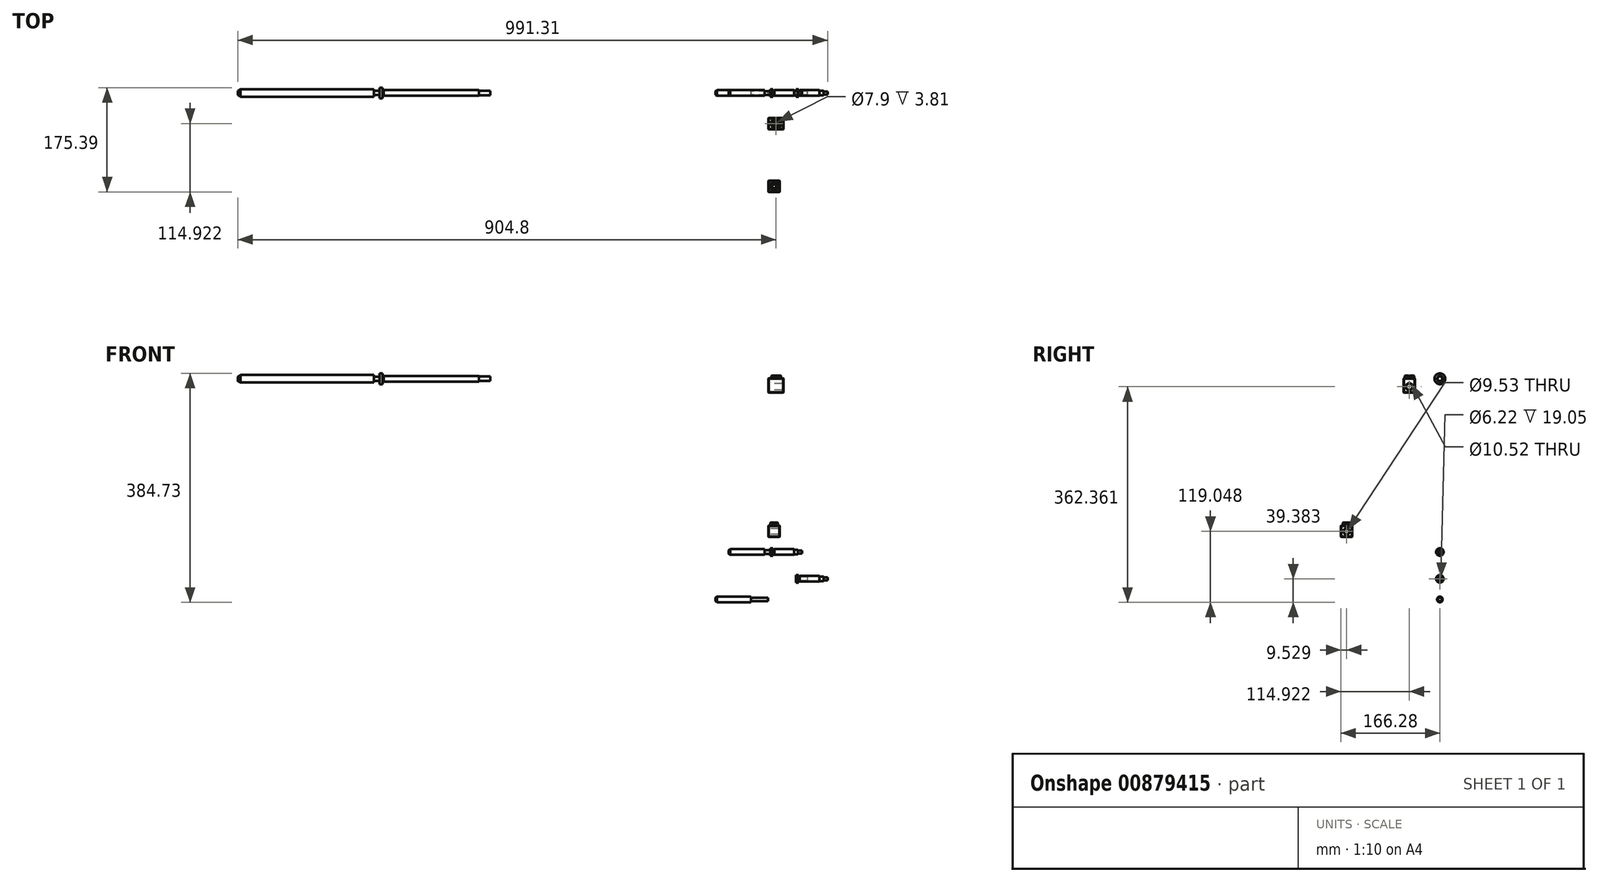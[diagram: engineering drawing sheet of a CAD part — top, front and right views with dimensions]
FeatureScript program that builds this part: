
annotation { "Feature Type Name" : "Feature", "Feature Type Description" : "" }
export const myFeature = defineFeature(function(context is Context, id is Id, definition is map)
    precondition{}
    {
        {
            var Q0;
            Q0=qCreatedBy(makeId("Front.planeOp"),FACE);
            var sketch = newSketch(context, id + "F0", { "sketchPlane" : qUnion([Q0])});
            skLineSegment(sketch, "E0", {"start": v(-67.18, -12.53) * mm, "end": v(-67.18, -9.42) * mm});
            skLineSegment(sketch, "E1", {"start": v(-67.18, -9.42) * mm, "end": v(-64.32, -7.77) * mm});
            skLineSegment(sketch, "E2", {"start": v(-64.32, -7.77) * mm, "end": v(-6.52, -7.77) * mm});
            skLineSegment(sketch, "E3", {"start": v(-6.52, -7.77) * mm, "end": v(-6.52, -9.42) * mm});
            skLineSegment(sketch, "E4", {"start": v(-6.52, -9.42) * mm, "end": v(2.67, -9.42) * mm});
            skLineSegment(sketch, "E5", {"start": v(2.67, -9.42) * mm, "end": v(2.67, -6.18) * mm});
            skLineSegment(sketch, "E6", {"start": v(2.67, -6.18) * mm, "end": v(7.44, -6.18) * mm});
            skLineSegment(sketch, "E7", {"start": v(7.44, -6.18) * mm, "end": v(7.44, -8.17) * mm});
            skLineSegment(sketch, "E8", {"start": v(7.44, -8.17) * mm, "end": v(9.6, -8.17) * mm});
            skLineSegment(sketch, "E9", {"start": v(9.6, -8.17) * mm, "end": v(9.6, -7.77) * mm});
            skLineSegment(sketch, "E10", {"start": v(9.6, -7.77) * mm, "end": v(42.62, -7.77) * mm});
            skLineSegment(sketch, "E11", {"start": v(42.62, -7.77) * mm, "end": v(42.62, -8.53) * mm});
            skLineSegment(sketch, "E12", {"start": v(42.62, -8.53) * mm, "end": v(49.47, -8.53) * mm});
            skLineSegment(sketch, "E13", {"start": v(56.08, -12.53) * mm, "end": v(-67.18, -12.53) * mm});
            skLineSegment(sketch, "E14", {"start": v(-6.52, -9.42) * mm, "end": v(-67.18, -9.42) * mm, "construction": true});
            skLineSegment(sketch, "E15", {"start": v(-6.52, -9.42) * mm, "end": v(-6.52, -12.53) * mm, "construction": true});
            skLineSegment(sketch, "E16", {"start": v(2.67, -9.42) * mm, "end": v(2.67, -12.53) * mm, "construction": true});
            skLineSegment(sketch, "E17", {"start": v(9.6, -8.17) * mm, "end": v(9.6, -12.53) * mm, "construction": true});
            skLineSegment(sketch, "E18", {"start": v(49.47, -8.53) * mm, "end": v(49.47, -9.8) * mm});
            skLineSegment(sketch, "E19", {"start": v(49.47, -9.8) * mm, "end": v(56.08, -9.8) * mm});
            skLineSegment(sketch, "E20", {"start": v(56.08, -9.8) * mm, "end": v(56.08, -12.53) * mm});
            skLineSegment(sketch, "E21", {"start": v(42.62, -8.53) * mm, "end": v(42.62, -12.53) * mm, "construction": true});
            skLineSegment(sketch, "E22", {"start": v(7.44, -8.17) * mm, "end": v(7.44, -12.53) * mm, "construction": true});
            skLineSegment(sketch, "E23", {"start": v(49.47, -9.8) * mm, "end": v(49.47, -12.53) * mm, "construction": true});
            skLineSegment(sketch, "E24", {"start": v(-89.3, -92.27) * mm, "end": v(-89.3, -89.15) * mm});
            skLineSegment(sketch, "E25", {"start": v(-89.3, -89.15) * mm, "end": v(-86.44, -87.5) * mm});
            skLineSegment(sketch, "E26", {"start": v(-86.44, -87.5) * mm, "end": v(-29.48, -87.5) * mm});
            skLineSegment(sketch, "E27", {"start": v(-29.48, -87.5) * mm, "end": v(-29.48, -89.15) * mm});
            skLineSegment(sketch, "E28", {"start": v(-29.48, -89.15) * mm, "end": v(-1.24, -89.15) * mm});
            skLineSegment(sketch, "E29", {"start": v(-29.48, -89.15) * mm, "end": v(-89.3, -89.15) * mm, "construction": true});
            skLineSegment(sketch, "E30", {"start": v(-89.3, -92.27) * mm, "end": v(-1.24, -92.27) * mm});
            skLineSegment(sketch, "E31", {"start": v(-1.24, -92.27) * mm, "end": v(-1.24, -89.15) * mm});
            skLineSegment(sketch, "E32", {"start": v(-86.44, -87.5) * mm, "end": v(-86.44, -92.27) * mm, "construction": true});
            skLineSegment(sketch, "E33", {"start": v(45.8, -54.54) * mm, "end": v(45.8, -51.3) * mm});
            skLineSegment(sketch, "E34", {"start": v(45.8, -51.3) * mm, "end": v(50.57, -51.3) * mm});
            skLineSegment(sketch, "E35", {"start": v(50.57, -51.3) * mm, "end": v(50.57, -53.28) * mm});
            skLineSegment(sketch, "E36", {"start": v(50.57, -53.28) * mm, "end": v(52.73, -53.28) * mm});
            skLineSegment(sketch, "E37", {"start": v(52.73, -53.28) * mm, "end": v(52.73, -52.88) * mm});
            skLineSegment(sketch, "E38", {"start": v(52.73, -52.88) * mm, "end": v(85.75, -52.88) * mm});
            skLineSegment(sketch, "E39", {"start": v(85.75, -53.65) * mm, "end": v(85.75, -52.88) * mm});
            skLineSegment(sketch, "E40", {"start": v(85.75, -53.65) * mm, "end": v(92.6, -53.65) * mm});
            skLineSegment(sketch, "E41", {"start": v(92.6, -53.65) * mm, "end": v(92.6, -54.92) * mm});
            skLineSegment(sketch, "E42", {"start": v(92.6, -54.92) * mm, "end": v(99.21, -54.92) * mm});
            skLineSegment(sketch, "E43", {"start": v(99.21, -54.92) * mm, "end": v(99.21, -57.65) * mm});
            skLineSegment(sketch, "E44", {"start": v(85.75, -53.65) * mm, "end": v(85.75, -57.65) * mm, "construction": true});
            skLineSegment(sketch, "E45", {"start": v(92.6, -54.92) * mm, "end": v(92.6, -57.65) * mm, "construction": true});
            skLineSegment(sketch, "E46", {"start": v(45.8, -54.54) * mm, "end": v(64.86, -54.54) * mm});
            skLineSegment(sketch, "E47", {"start": v(64.86, -54.54) * mm, "end": v(64.86, -57.65) * mm});
            skLineSegment(sketch, "E48.trimOffspring", {"start": v(64.86, -57.65) * mm, "end": v(99.21, -57.65) * mm});
            skLineSegment(sketch, "E49", {"start": v(45.8, -54.54) * mm, "end": v(45.8, -57.65) * mm, "construction": true});
            skLineSegment(sketch, "E50", {"start": v(45.8, -57.65) * mm, "end": v(64.86, -57.65) * mm, "construction": true});
            skSolve(sketch);
        }
        {
            var Q0;
            Q0=makeQuery(id+"F0.imprint","IMPRINT",FACE,{"disambiguationData":[TD([[makeQuery(id+"F0.imprint","IMPRINT",EDGE,{"derivedFrom":sQuery(id+"F0.wireOp",EDGE,"E0")}),-1.0]])]});
            var Q1;
            Q1=sQuery(id+"F0.wireOp",EDGE,"E13");
            revolve(context, id + "F1", {"surfaceOperationType" : NewSurfaceOperationType.NEW, "entities" : qUnion([Q0]), "axis" : qUnion([Q1]), "revolveType" : RevolveType.FULL});
        }
        {
            var Q0;
            Q0=makeQuery(id+"F0.imprint","IMPRINT",FACE,{"disambiguationData":[TD([[makeQuery(id+"F0.imprint","IMPRINT",EDGE,{"derivedFrom":sQuery(id+"F0.wireOp",EDGE,"E24")}),-1.0]])]});
            var Q1;
            Q1=sQuery(id+"F0.wireOp",EDGE,"E30");
            revolve(context, id + "F2", {"surfaceOperationType" : NewSurfaceOperationType.NEW, "entities" : qUnion([Q0]), "axis" : qUnion([Q1]), "revolveType" : RevolveType.FULL});
        }
        {
            var Q0;
            Q0=makeQuery(id+"F0.imprint","IMPRINT",FACE,{"disambiguationData":[TD([[makeQuery(id+"F0.imprint","IMPRINT",EDGE,{"derivedFrom":sQuery(id+"F0.wireOp",EDGE,"E33")}),-1.0]])]});
            var Q1;
            Q1=sQuery(id+"F0.wireOp",EDGE,"E48.trimOffspring");
            revolve(context, id + "F3", {"surfaceOperationType" : NewSurfaceOperationType.NEW, "entities" : qUnion([Q0]), "axis" : qUnion([Q1]), "revolveType" : RevolveType.FULL});
        }
        {
            var Q0;
            Q0=qCreatedBy(makeId("Right.planeOp"),FACE);
            var sketch = newSketch(context, id + "F4", { "sketchPlane" : qUnion([Q0])});
            skCircle(sketch, "E51", {"center": v(-156.75, 22.02) * mm, "radius": 4.76 * mm});
            skLineSegment(sketch, "E52.bottom", {"start": v(-166.28, 31.54) * mm, "end": v(-147.23, 31.54) * mm});
            skLineSegment(sketch, "E52.top", {"start": v(-166.28, 12.5) * mm, "end": v(-147.23, 12.5) * mm});
            skLineSegment(sketch, "E52.left", {"start": v(-166.28, 31.54) * mm, "end": v(-166.28, 12.5) * mm});
            skLineSegment(sketch, "E52.right", {"start": v(-147.23, 31.54) * mm, "end": v(-147.23, 12.5) * mm});
            skLineSegment(sketch, "E53", {"start": v(-166.28, 31.54) * mm, "end": v(-147.23, 12.5) * mm, "construction": true});
            skSolve(sketch);
        }
        {
            var Q0;
            Q0=makeQuery(id+"F4.imprint","IMPRINT",FACE,{"disambiguationData":[TD([[makeQuery(id+"F4.imprint","IMPRINT",EDGE,{"derivedFrom":sQuery(id+"F4.wireOp",EDGE,"E51")}),-1.0]])]});
            extrude(context, id + "F5", {"entities" : qUnion([Q0]), "depth" : 19.05 * mm, "offsetDistance" : 25.4 * mm});
        }
        {
            var Q0;
            Q0=makeQuery(id+"F5.opExtrude","SWEPT_FACE",FACE,{"disambiguationData":[OSD([sQuery(id+"F4.wireOp",EDGE,"E52.bottom")])]});
            var sketch = newSketch(context, id + "F6", { "sketchPlane" : qUnion([Q0])});
            skLineSegment(sketch, "E54", {"start": v(0, -147.23) * mm, "end": v(19.05, -166.28) * mm, "construction": true});
            skCircle(sketch, "E55", {"center": v(9.53, -156.75) * mm, "radius": 6.35 * mm});
            skCircle(sketch, "E56", {"center": v(9.53, -156.75) * mm, "radius": 3.18 * mm});
            skSolve(sketch);
        }
        {
            var Q0;
            Q0=makeQuery(id+"F6.imprint","IMPRINT",FACE,{"disambiguationData":[TD([[makeQuery(id+"F6.imprint","IMPRINT",EDGE,{"derivedFrom":sQuery(id+"F6.wireOp",EDGE,"E55")}),1.0]])]});
            extrude(context, id + "F7", {"entities" : qUnion([Q0]), "operationType" : NewBodyOperationType.ADD, "depth" : 5.08 * mm, "offsetDistance" : 25.4 * mm});
        }
        {
            var Q0;
            Q0=makeQuery(id+"F7.opExtrude","CAP_EDGE",EDGE,{"disambiguationData":[OSD([sQuery(id+"F6.wireOp",EDGE,"E55")])],"isStart":false});
            var Q1;
            Q1=makeQuery(id+"F7.opExtrude","CAP_EDGE",EDGE,{"disambiguationData":[OSD([sQuery(id+"F6.wireOp",EDGE,"E56")])],"isStart":false});
            var Q2;
            Q2=makeQuery(id+"F5.opExtrude","CAP_EDGE",EDGE,{"disambiguationData":[OSD([sQuery(id+"F4.wireOp",EDGE,"E51")])],"isStart":false});
            var Q3;
            Q3=makeQuery(id+"F5.opExtrude","CAP_EDGE",EDGE,{"disambiguationData":[OSD([sQuery(id+"F4.wireOp",EDGE,"E52.bottom")])],"isStart":false});
            var Q4;
            {var subQ0=sQuery(id+"F4.wireOp",EDGE,"E52.left");var subQ3=sQuery(id+"F4.wireOp",EDGE,"E52.bottom");Q4=makeQuery(id+"F7.boolean.opBoolean","SPLIT",FACE,{"disambiguationData":[TD([makeQuery(id+"F5.opExtrude","SWEPT_FACE",FACE,{"disambiguationData":[OSD([subQ0])]})])],"derivedFrom":makeQuery(id+"F5.opExtrude","SWEPT_FACE",FACE,{"disambiguationData":[OSD([subQ3])]})});}
            var Q5;
            Q5=makeQuery(id+"F5.opExtrude","SWEPT_FACE",FACE,{"disambiguationData":[OSD([sQuery(id+"F4.wireOp",EDGE,"E52.right")])]});
            var Q6;
            Q6=makeQuery(id+"F5.opExtrude","CAP_FACE",FACE,{"disambiguationData":[OSD([sQuery(id+"F4.wireOp",EDGE,"E51"),sQuery(id+"F4.wireOp",EDGE,"E52.bottom"),sQuery(id+"F4.wireOp",EDGE,"E52.top"),sQuery(id+"F4.wireOp",EDGE,"E52.left"),sQuery(id+"F4.wireOp",EDGE,"E52.right")])],"isStart":false});
            var Q7;
            Q7=makeQuery(id+"F5.opExtrude","SWEPT_FACE",FACE,{"disambiguationData":[OSD([sQuery(id+"F4.wireOp",EDGE,"E52.left")])]});
            var Q8;
            Q8=makeQuery(id+"F5.opExtrude","CAP_FACE",FACE,{"disambiguationData":[OSD([sQuery(id+"F4.wireOp",EDGE,"E51"),sQuery(id+"F4.wireOp",EDGE,"E52.bottom"),sQuery(id+"F4.wireOp",EDGE,"E52.top"),sQuery(id+"F4.wireOp",EDGE,"E52.left"),sQuery(id+"F4.wireOp",EDGE,"E52.right")])],"isStart":true});
            chamfer(context, id + "F8", {"entities" : qUnion([Q0, Q1, Q2, Q3, Q4, Q5, Q6, Q7, Q8]), "width" : 0.64 * mm, "tangentPropagation" : true});
        }
        {
            var Q0;
            Q0=qCreatedBy(makeId("Front.planeOp"),FACE);
            var sketch = newSketch(context, id + "F9", { "sketchPlane" : qUnion([Q0])});
            skLineSegment(sketch, "E57", {"start": v(-892.1, 278.6) * mm, "end": v(-892.1, 282.16) * mm});
            skLineSegment(sketch, "E58", {"start": v(-892.1, 282.16) * mm, "end": v(-887.29, 284.95) * mm});
            skLineSegment(sketch, "E59", {"start": v(-887.29, 284.95) * mm, "end": v(-663.5, 284.95) * mm});
            skLineSegment(sketch, "E60", {"start": v(-663.5, 284.95) * mm, "end": v(-663.5, 282.16) * mm});
            skLineSegment(sketch, "E61", {"start": v(-663.5, 282.16) * mm, "end": v(-653.98, 282.16) * mm});
            skLineSegment(sketch, "E62", {"start": v(-653.98, 282.16) * mm, "end": v(-653.98, 287.7) * mm});
            skLineSegment(sketch, "E63", {"start": v(-653.98, 287.7) * mm, "end": v(-648.9, 287.7) * mm});
            skLineSegment(sketch, "E64", {"start": v(-648.9, 287.7) * mm, "end": v(-648.9, 282.99) * mm});
            skLineSegment(sketch, "E65", {"start": v(-648.9, 282.99) * mm, "end": v(-646.74, 282.99) * mm});
            skLineSegment(sketch, "E66", {"start": v(-646.74, 283.36) * mm, "end": v(-486.97, 283.36) * mm});
            skLineSegment(sketch, "E67", {"start": v(-467.92, 278.6) * mm, "end": v(-892.1, 278.6) * mm});
            skLineSegment(sketch, "E68", {"start": v(-663.5, 282.16) * mm, "end": v(-892.1, 282.16) * mm, "construction": true});
            skLineSegment(sketch, "E69", {"start": v(-663.5, 282.16) * mm, "end": v(-663.5, 278.6) * mm, "construction": true});
            skLineSegment(sketch, "E70", {"start": v(-653.98, 282.16) * mm, "end": v(-653.98, 278.6) * mm, "construction": true});
            skLineSegment(sketch, "E71", {"start": v(-646.74, 282.99) * mm, "end": v(-646.74, 278.6) * mm, "construction": true});
            skLineSegment(sketch, "E72", {"start": v(-486.97, 283.36) * mm, "end": v(-486.97, 282.43) * mm});
            skLineSegment(sketch, "E73", {"start": v(-486.97, 282.43) * mm, "end": v(-467.92, 282.43) * mm});
            skLineSegment(sketch, "E74", {"start": v(-467.92, 282.43) * mm, "end": v(-467.92, 278.6) * mm});
            skLineSegment(sketch, "E75", {"start": v(-648.9, 282.99) * mm, "end": v(-648.9, 278.6) * mm, "construction": true});
            skLineSegment(sketch, "E76", {"start": v(-486.97, 282.43) * mm, "end": v(-486.97, 278.6) * mm, "construction": true});
            skLineSegment(sketch, "E77", {"start": v(-646.74, 283.36) * mm, "end": v(-646.74, 282.99) * mm});
            skSolve(sketch);
        }
        {
            var Q0;
            Q0=makeQuery(id+"F9.imprint","IMPRINT",FACE,{"disambiguationData":[TD([[makeQuery(id+"F9.imprint","IMPRINT",EDGE,{"derivedFrom":sQuery(id+"F9.wireOp",EDGE,"E57")}),-1.0]])]});
            var Q1;
            Q1=sQuery(id+"F9.wireOp",EDGE,"E67");
            revolve(context, id + "F10", {"surfaceOperationType" : NewSurfaceOperationType.NEW, "entities" : qUnion([Q0]), "axis" : qUnion([Q1]), "revolveType" : RevolveType.FULL});
        }
        {
            var Q0;
            Q0=qCreatedBy(makeId("Right.planeOp"),FACE);
            var sketch = newSketch(context, id + "F11", { "sketchPlane" : qUnion([Q0])});
            skLineSegment(sketch, "E78.bottom", {"start": v(-60.95, 279.68) * mm, "end": v(-41.77, 279.68) * mm});
            skLineSegment(sketch, "E78.top", {"start": v(-60.95, 255.55) * mm, "end": v(-41.77, 255.55) * mm});
            skLineSegment(sketch, "E78.left", {"start": v(-60.95, 279.68) * mm, "end": v(-60.95, 255.55) * mm});
            skLineSegment(sketch, "E78.right", {"start": v(-41.77, 279.68) * mm, "end": v(-41.77, 255.55) * mm});
            skCircle(sketch, "E79", {"center": v(-51.36, 265.33) * mm, "radius": 5.26 * mm});
            skLineSegment(sketch, "E80", {"start": v(-51.36, 265.33) * mm, "end": v(-51.36, 279.68) * mm, "construction": true});
            skSolve(sketch);
        }
        {
            var Q0;
            Q0=makeQuery(id+"F11.imprint","IMPRINT",FACE,{"disambiguationData":[TD([[makeQuery(id+"F11.imprint","IMPRINT",EDGE,{"derivedFrom":sQuery(id+"F11.wireOp",EDGE,"E78.bottom")}),-1.0]])]});
            extrude(context, id + "F12", {"entities" : qUnion([Q0]), "depth" : 25.4 * mm, "offsetDistance" : 25.4 * mm});
        }
        {
            var Q0;
            Q0=makeQuery(id+"F12.opExtrude","SWEPT_FACE",FACE,{"disambiguationData":[OSD([sQuery(id+"F11.wireOp",EDGE,"E78.bottom")])]});
            var sketch = newSketch(context, id + "F13", { "sketchPlane" : qUnion([Q0])});
            skLineSegment(sketch, "E81", {"start": v(0, -41.77) * mm, "end": v(25.4, -60.95) * mm, "construction": true});
            skCircle(sketch, "E82", {"center": v(12.7, -51.36) * mm, "radius": 7.91 * mm});
            skCircle(sketch, "E83", {"center": v(12.7, -51.36) * mm, "radius": 3.95 * mm});
            skSolve(sketch);
        }
        {
            var Q0;
            Q0=makeQuery(id+"F13.imprint","IMPRINT",FACE,{"disambiguationData":[TD([[makeQuery(id+"F13.imprint","IMPRINT",EDGE,{"derivedFrom":sQuery(id+"F13.wireOp",EDGE,"E82")}),1.0]])]});
            extrude(context, id + "F14", {"entities" : qUnion([Q0]), "operationType" : NewBodyOperationType.ADD, "depth" : 4.44 * mm, "offsetDistance" : 25.4 * mm});
        }
        {
            var Q0;
            Q0=makeQuery(id+"F14.opExtrude","CAP_FACE",FACE,{"disambiguationData":[OSD([sQuery(id+"F13.wireOp",EDGE,"E82"),sQuery(id+"F13.wireOp",EDGE,"E83")])],"isStart":false});
            var Q1;
            {var subQ1=sQuery(id+"F11.wireOp",EDGE,"E78.left");var subQ4=sQuery(id+"F11.wireOp",EDGE,"E78.bottom");Q1=makeQuery(id+"F14.boolean.opBoolean","SPLIT",FACE,{"disambiguationData":[TD([makeQuery(id+"F12.opExtrude","SWEPT_FACE",FACE,{"disambiguationData":[OSD([subQ1])]})])],"derivedFrom":makeQuery(id+"F12.opExtrude","SWEPT_FACE",FACE,{"disambiguationData":[OSD([subQ4])]})});}
            var Q2;
            Q2=makeQuery(id+"F12.opExtrude","CAP_FACE",FACE,{"disambiguationData":[OSD([sQuery(id+"F11.wireOp",EDGE,"E78.bottom"),sQuery(id+"F11.wireOp",EDGE,"E78.top"),sQuery(id+"F11.wireOp",EDGE,"E78.left"),sQuery(id+"F11.wireOp",EDGE,"E78.right"),sQuery(id+"F11.wireOp",EDGE,"E79")])],"isStart":true});
            var Q3;
            Q3=makeQuery(id+"F12.opExtrude","SWEPT_FACE",FACE,{"disambiguationData":[OSD([sQuery(id+"F11.wireOp",EDGE,"E78.right")])]});
            var Q4;
            Q4=makeQuery(id+"F12.opExtrude","CAP_FACE",FACE,{"disambiguationData":[OSD([sQuery(id+"F11.wireOp",EDGE,"E78.bottom"),sQuery(id+"F11.wireOp",EDGE,"E78.top"),sQuery(id+"F11.wireOp",EDGE,"E78.left"),sQuery(id+"F11.wireOp",EDGE,"E78.right"),sQuery(id+"F11.wireOp",EDGE,"E79")])],"isStart":false});
            var Q5;
            Q5=makeQuery(id+"F12.opExtrude","SWEPT_FACE",FACE,{"disambiguationData":[OSD([sQuery(id+"F11.wireOp",EDGE,"E78.left")])]});
            chamfer(context, id + "F15", {"entities" : qUnion([Q0, Q1, Q2, Q3, Q4, Q5]), "width" : 0.64 * mm, "tangentPropagation" : true});
        }
    });
